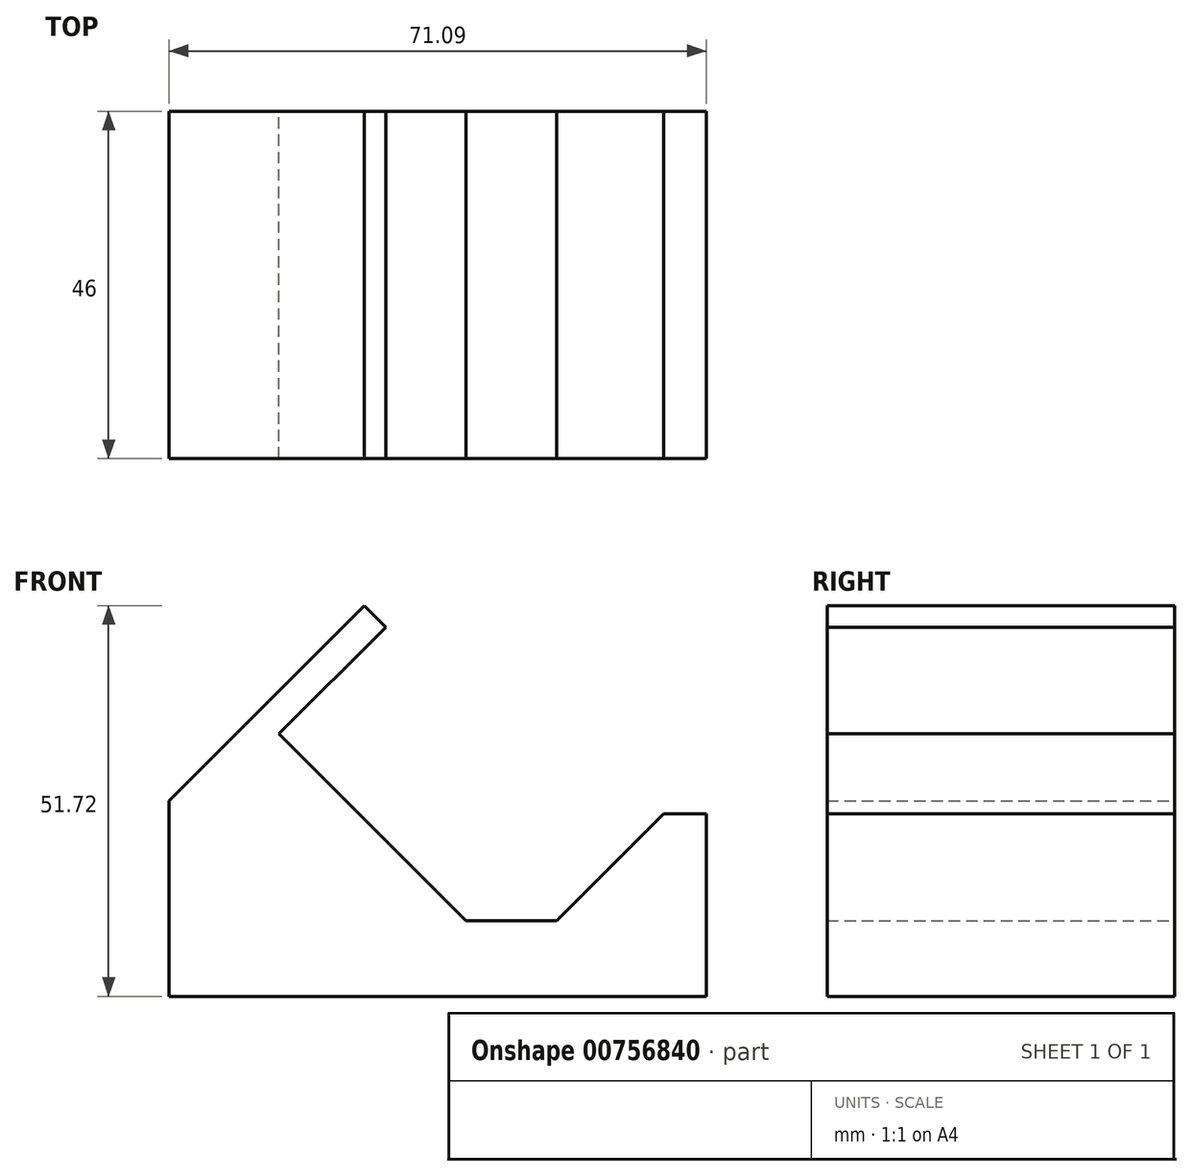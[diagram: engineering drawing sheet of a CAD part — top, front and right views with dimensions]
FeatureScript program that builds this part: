
annotation { "Feature Type Name" : "Feature", "Feature Type Description" : "" }
export const myFeature = defineFeature(function(context is Context, id is Id, definition is map)
    precondition{}
    {
        {
            var Q0;
            Q0=qCreatedBy(makeId("Front.planeOp"),FACE);
            var sketch = newSketch(context, id + "F0", { "sketchPlane" : qUnion([Q0])});
            skLineSegment(sketch, "E0", {"start": v(40, 0) * mm, "end": v(54.14, 14.14) * mm});
            skLineSegment(sketch, "E1", {"start": v(54.14, 14.14) * mm, "end": v(59.8, 14.14) * mm});
            skLineSegment(sketch, "E2", {"start": v(40, 0) * mm, "end": v(28, 0) * mm});
            skLineSegment(sketch, "E3", {"start": v(0, 0) * mm, "end": v(-0.28, 0) * mm});
            skLineSegment(sketch, "E4", {"start": v(59.8, 14.14) * mm, "end": v(59.8, -10) * mm});
            skLineSegment(sketch, "E5", {"start": v(28, 0) * mm, "end": v(3.25, 24.75) * mm});
            skLineSegment(sketch, "E6", {"start": v(3.25, 24.75) * mm, "end": v(17.4, 38.9) * mm});
            skLineSegment(sketch, "E7", {"start": v(17.4, 38.9) * mm, "end": v(14.56, 41.72) * mm});
            skLineSegment(sketch, "E8", {"start": v(14.56, 41.72) * mm, "end": v(-11.3, 15.86) * mm});
            skLineSegment(sketch, "E9", {"start": v(59.8, -10) * mm, "end": v(-11.3, -10) * mm});
            skLineSegment(sketch, "E10", {"start": v(-11.3, 15.86) * mm, "end": v(-11.3, -10) * mm});
            skSolve(sketch);
        }
        {
            var Q0;
            Q0=makeQuery(id+"F0.imprint","IMPRINT",FACE,{"disambiguationData":[TD([[makeQuery(id+"F0.imprint","IMPRINT",EDGE,{"derivedFrom":sQuery(id+"F0.wireOp",EDGE,"lcIFVH9Y-AtUo-1AhQ-khoD-9LlUAWvDUtTh")}),-1.0]])]});
            var Q1;
            Q1=makeQuery(id+"F0.imprint","IMPRINT",FACE,{"disambiguationData":[TD([[makeQuery(id+"F0.imprint","IMPRINT",EDGE,{"derivedFrom":sQuery(id+"F0.wireOp",EDGE,"f1f9418a-7414-447b-94d6-8a42a41ea951.0")}),-1.0]])]});
            var Q2;
            {var subQ0=sQuery(id+"F0.wireOp",EDGE,"pBqpSAaG-MMCg-se9h-RNcu-28PXkp3zBWMy");Q2=makeQuery(id+"F0.imprint","IMPRINT",FACE,{"disambiguationData":[TD([[makeQuery(id+"F0.imprint","IMPRINT",EDGE,{"derivedFrom":subQ0}),1.0]])]});}
            var Q3;
            {var subQ0=sQuery(id+"F0.wireOp",EDGE,"3DMmWTto-zGNs-5LsF-4088-LrQmxh5JYvqc");Q3=makeQuery(id+"F0.imprint","IMPRINT",FACE,{"disambiguationData":[TD([[makeQuery(id+"F0.imprint","IMPRINT",EDGE,{"derivedFrom":subQ0}),1.0]])]});}
            var Q4;
            {var subQ2=sQuery(id+"F0.wireOp",EDGE,"t2p0JqAR-NOjC-uep4-4t9G-0nvLcHitK0lN");Q4=makeQuery(id+"F0.imprint","IMPRINT",FACE,{"disambiguationData":[TD([[makeQuery(id+"F0.imprint","IMPRINT",EDGE,{"derivedFrom":subQ2}),-1.0]])]});}
            var Q5;
            {var subQ3=sQuery(id+"F0.wireOp",EDGE,"E0");Q5=makeQuery(id+"F0.imprint","IMPRINT",FACE,{"disambiguationData":[TD([[makeQuery(id+"F0.imprint","IMPRINT",EDGE,{"derivedFrom":subQ3}),-1.0]])]});}
            extrude(context, id + "F1", {"entities" : qUnion([Q0, Q1, Q2, Q3, Q4, Q5]), "depth" : 46 * mm, "offsetDistance" : 25 * mm});
        }
    });
